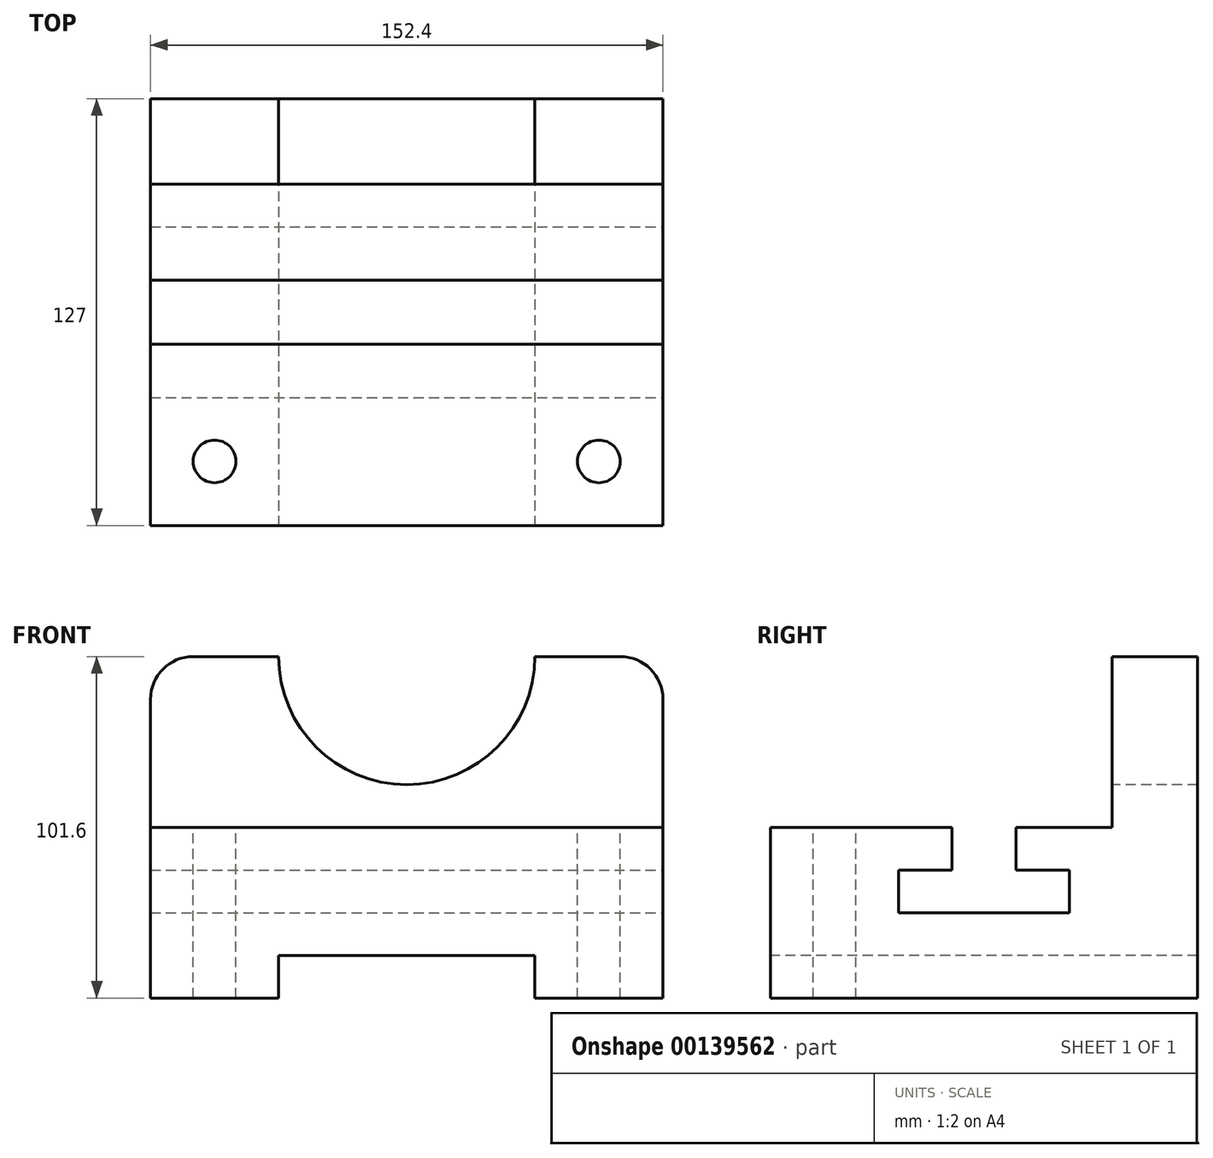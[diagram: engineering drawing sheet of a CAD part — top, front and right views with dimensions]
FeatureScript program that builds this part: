
annotation { "Feature Type Name" : "Feature", "Feature Type Description" : "" }
export const myFeature = defineFeature(function(context is Context, id is Id, definition is map)
    precondition{}
    {
        {
            var Q0;
            Q0=qCreatedBy(makeId("Right.planeOp"),FACE);
            var sketch = newSketch(context, id + "F0", { "sketchPlane" : qUnion([Q0])});
            skLineSegment(sketch, "E0", {"start": v(-127, 50.8) * mm, "end": v(-127, 0) * mm});
            skLineSegment(sketch, "E1", {"start": v(-127, 0) * mm, "end": v(0, 0) * mm});
            skLineSegment(sketch, "E2", {"start": v(0, 0) * mm, "end": v(0, 101.6) * mm});
            skLineSegment(sketch, "E3", {"start": v(-127, 50.8) * mm, "end": v(0, 50.8) * mm});
            skLineSegment(sketch, "E4", {"start": v(-73.03, 50.8) * mm, "end": v(-73.03, 38.1) * mm});
            skLineSegment(sketch, "E5", {"start": v(-73.03, 38.1) * mm, "end": v(-88.9, 38.1) * mm});
            skLineSegment(sketch, "E6", {"start": v(-88.9, 38.1) * mm, "end": v(-88.9, 25.4) * mm});
            skLineSegment(sketch, "E7", {"start": v(-88.9, 25.4) * mm, "end": v(-38.1, 25.4) * mm});
            skLineSegment(sketch, "E8", {"start": v(-38.1, 25.4) * mm, "end": v(-38.1, 38.1) * mm});
            skLineSegment(sketch, "E9", {"start": v(-38.1, 38.1) * mm, "end": v(-53.98, 38.1) * mm});
            skLineSegment(sketch, "E10", {"start": v(-53.98, 38.1) * mm, "end": v(-53.98, 50.8) * mm});
            skLineSegment(sketch, "E11", {"start": v(0, 101.6) * mm, "end": v(-25.4, 101.6) * mm});
            skLineSegment(sketch, "E12", {"start": v(-25.4, 101.6) * mm, "end": v(-25.4, 50.8) * mm});
            skSolve(sketch);
        }
        {
            var Q0;
            {var subQ0=sQuery(id+"F0.wireOp",EDGE,"E0");Q0=makeQuery(id+"F0.imprint","IMPRINT",FACE,{"disambiguationData":[TD([[makeQuery(id+"F0.imprint","IMPRINT",EDGE,{"derivedFrom":subQ0}),1.0]])]});}
            var Q1;
            {var subQ0=sQuery(id+"F0.wireOp",EDGE,"E11");Q1=makeQuery(id+"F0.imprint","IMPRINT",FACE,{"disambiguationData":[TD([[makeQuery(id+"F0.imprint","IMPRINT",EDGE,{"derivedFrom":subQ0}),1.0]])]});}
            extrude(context, id + "F1", {"entities" : qUnion([Q0, Q1]), "oppositeDirection" : true, "depth" : 152.4 * mm});
        }
        {
            var Q0;
            Q0=makeQuery(id+"F1.opExtrude","SWEPT_FACE",FACE,{"disambiguationData":[OSD([sQuery(id+"F0.wireOp",EDGE,"E0")])]});
            var sketch = newSketch(context, id + "F2", { "sketchPlane" : qUnion([Q0])});
            skLineSegment(sketch, "E13", {"start": v(-114.3, 0) * mm, "end": v(-114.3, 12.7) * mm});
            skLineSegment(sketch, "E14", {"start": v(-114.3, 12.7) * mm, "end": v(-38.1, 12.7) * mm});
            skLineSegment(sketch, "E15", {"start": v(-38.1, 12.7) * mm, "end": v(-38.1, 0) * mm});
            skSolve(sketch);
        }
        {
            var Q0;
            {var subQ0=sQuery(id+"F2.wireOp",EDGE,"E13");Q0=makeQuery(id+"F2.imprint","IMPRINT",FACE,{"disambiguationData":[TD([[makeQuery(id+"F2.imprint","IMPRINT",EDGE,{"derivedFrom":subQ0}),-1.0]])]});}
            extrude(context, id + "F3", {"entities" : qUnion([Q0]), "operationType" : NewBodyOperationType.REMOVE, "endBound" : BoundingType.THROUGH_ALL, "oppositeDirection" : true, "depth" : 25.4 * mm});
        }
        {
            var Q0;
            Q0=makeQuery(id+"F1.opExtrude","CAP_EDGE",EDGE,{"disambiguationData":[OSD([sQuery(id+"F0.wireOp",EDGE,"E11")])],"isStart":true});
            var Q1;
            Q1=makeQuery(id+"F1.opExtrude","CAP_EDGE",EDGE,{"disambiguationData":[OSD([sQuery(id+"F0.wireOp",EDGE,"E11")])],"isStart":false});
            fillet(context, id + "F4", {"entities" : qUnion([Q0, Q1]), "radius" : 12.7 * mm, "tangentPropagation" : true, "allowEdgeOverflow" : false});
        }
        {
            var Q0;
            {var subQ0=sQuery(id+"F0.wireOp",EDGE,"E3");Q0=makeQuery(id+"F1.opExtrude","SWEPT_FACE",FACE,{"disambiguationData":[OSD([subQ0]),TDD([makeQuery(id+"F0.imprint","IMPRINT",EDGE,{"disambiguationData":[TD([[makeQuery(id+"F0.imprint","INTERSECT",VERTEX,{"derivedFrom":[sQuery(id+"F0.wireOp",EDGE,"E0"),subQ0]}),-1.0]])],"derivedFrom":subQ0})])]});}
            var sketch = newSketch(context, id + "F5", { "sketchPlane" : qUnion([Q0])});
            skCircle(sketch, "E16", {"center": v(-133.35, -107.95) * mm, "radius": 6.35 * mm});
            skCircle(sketch, "E17", {"center": v(-19.05, -107.95) * mm, "radius": 6.35 * mm});
            skSolve(sketch);
        }
        {
            var Q0;
            Q0 = qSketchRegion(id + "F5", true);
            extrude(context, id + "F6", {"entities" : qUnion([Q0]), "operationType" : NewBodyOperationType.REMOVE, "endBound" : BoundingType.THROUGH_ALL, "oppositeDirection" : true, "depth" : 25.4 * mm});
        }
        {
            var Q0;
            Q0=makeQuery(id+"F1.opExtrude","SWEPT_FACE",FACE,{"disambiguationData":[OSD([sQuery(id+"F0.wireOp",EDGE,"E12")])]});
            var sketch = newSketch(context, id + "F7", { "sketchPlane" : qUnion([Q0])});
            skCircle(sketch, "E18", {"center": v(-76.2, 101.6) * mm, "radius": 38.1 * mm});
            skSolve(sketch);
        }
        {
            var Q0;
            Q0 = qSketchRegion(id + "F7", true);
            extrude(context, id + "F8", {"entities" : qUnion([Q0]), "operationType" : NewBodyOperationType.REMOVE, "endBound" : BoundingType.THROUGH_ALL, "oppositeDirection" : true, "depth" : 25.4 * mm});
        }
    });
